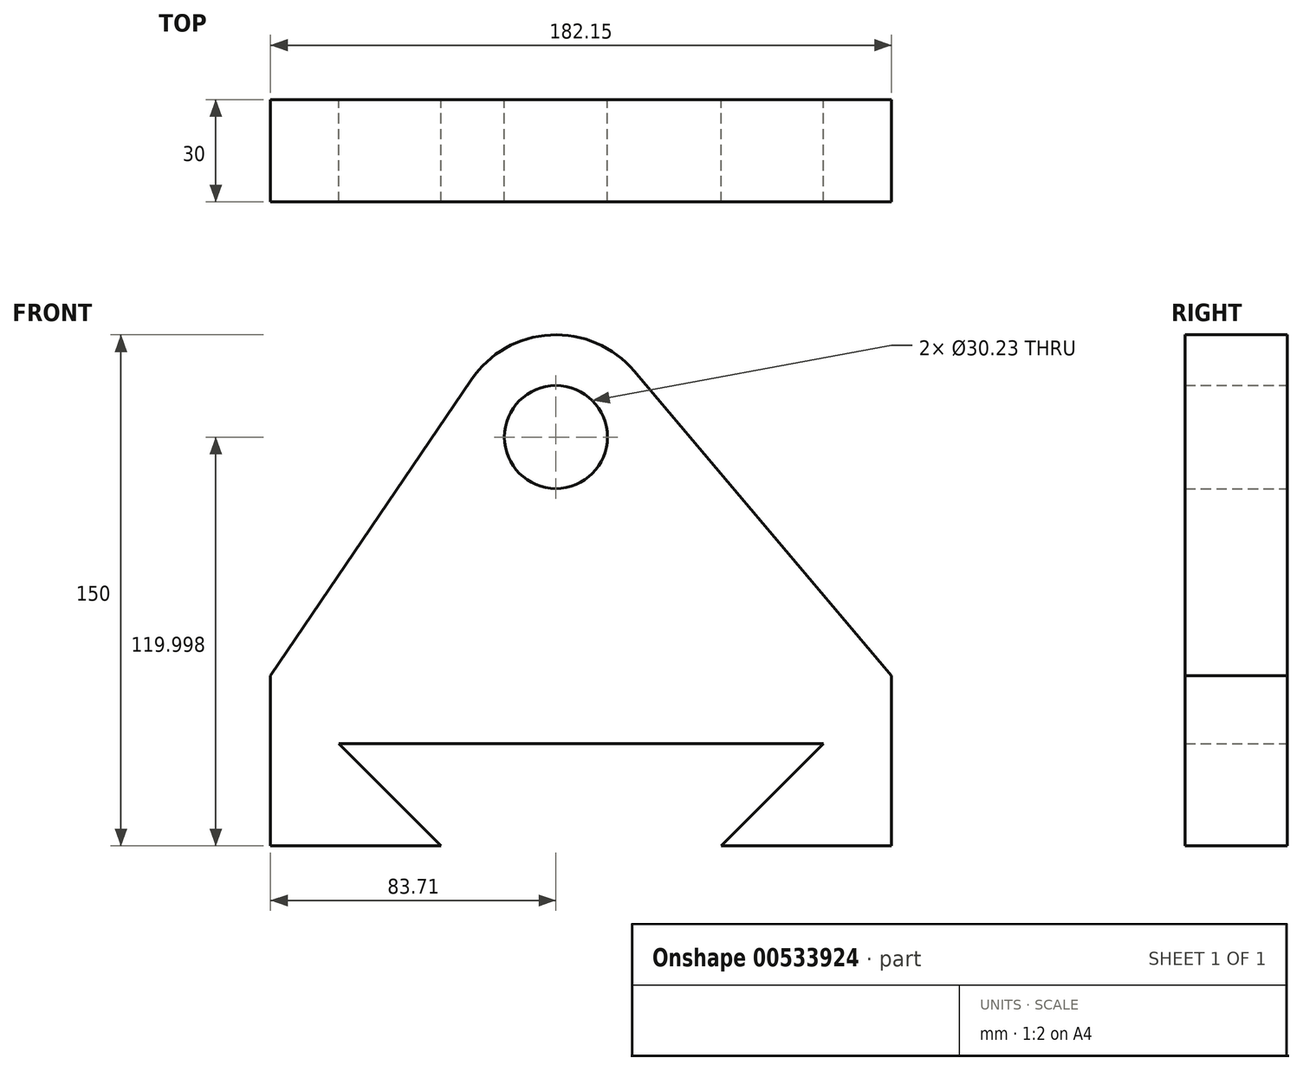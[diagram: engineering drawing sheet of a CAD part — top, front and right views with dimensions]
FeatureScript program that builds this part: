
annotation { "Feature Type Name" : "Feature", "Feature Type Description" : "" }
export const myFeature = defineFeature(function(context is Context, id is Id, definition is map)
    precondition{}
    {
        {
            var Q0;
            Q0=qCreatedBy(makeId("Front.planeOp"),FACE);
            var sketch = newSketch(context, id + "F0", { "sketchPlane" : qUnion([Q0])});
            skCircle(sketch, "E0", {"center": v(0, 41.3) * mm, "radius": 30 * mm});
            skLineSegment(sketch, "E1", {"start": v(-83.7, -28.7) * mm, "end": v(98.44, -28.7) * mm});
            skLineSegment(sketch, "E2", {"start": v(-83.7, -28.7) * mm, "end": v(-83.7, -78.7) * mm});
            skLineSegment(sketch, "E3", {"start": v(98.44, -28.7) * mm, "end": v(98.44, -78.7) * mm});
            skLineSegment(sketch, "E4", {"start": v(98.44, -78.7) * mm, "end": v(48.44, -78.7) * mm});
            skLineSegment(sketch, "E5", {"start": v(-83.7, -78.7) * mm, "end": v(-33.7, -78.7) * mm});
            skLineSegment(sketch, "E6", {"start": v(48.44, -78.7) * mm, "end": v(78.44, -48.7) * mm});
            skLineSegment(sketch, "E7", {"start": v(78.44, -48.7) * mm, "end": v(-63.7, -48.7) * mm});
            skCircle(sketch, "E8", {"center": v(0, 41.3) * mm, "radius": 15.12 * mm});
            skLineSegment(sketch, "E9", {"start": v(-63.7, -48.7) * mm, "end": v(-33.7, -78.7) * mm});
            skLineSegment(sketch, "E10", {"start": v(-83.7, -28.7) * mm, "end": v(-24.83, 58.14) * mm});
            skLineSegment(sketch, "E11", {"start": v(22.91, 60.67) * mm, "end": v(98.44, -28.7) * mm});
            skSolve(sketch);
        }
        {
            var Q0;
            Q0 = qSketchRegion(id + "F0", true);
            extrude(context, id + "F1", {"entities" : qUnion([Q0]), "depth" : 30 * mm, "offsetDistance" : 25 * mm});
        }
    });
